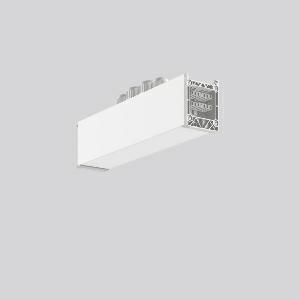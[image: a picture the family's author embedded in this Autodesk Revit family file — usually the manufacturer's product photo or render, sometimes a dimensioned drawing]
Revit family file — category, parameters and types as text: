
# Revit family: linedo_mitteleinspeisung_14pol_b_b_982698_002_1_c4a3
name_source: partatom
category: Lighting Fixtures
units: mm (PartAtom-declared; Revit-internal decimal feet)

## family parameters
Cut with Voids When Loaded = No
Host = Face
Light Source = No
Part Type = Normal
Room Calculation Point = No
Round Connector Dimension = Use Diameter
Shared = No

## types (1)
- LINEDO_Mitteleinspeisung_14pol_B_B
    Apparent Load = 0 VA
    Default Elevation = 1800 mm
    Description = Series: LINEDO
Middle power feed, 14-pole, connection socket / socket. Housing: extruded aluminium profile, powder-coated. Cover made of plastic, surface like housing. LINEDO plug system, plastic, light grey. 4 cable glands (2 x M20 and 2 x M25). Cable glands on top. Easy connection for rigid or flexible wires.
Colour: white
Length: 312 mm
Width: 58 mm
Height: 76 mm
Weight: 850 g
    Height = 76 mm
    Lamp = 0 x
    Length = 312 mm
    Luminous efficacy = 0 lm/W
    Manufacturer = RZB
    ModVariant = No
    Model = 982698.002.1
    Mounting Place = Ceiling
    Mounting Type = Surface mounted, Pendant
    Number of Poles = 1
    OnlyDefault = Yes
    Power Factor = 1
    Product Name = LINEDO_Mitteleinspeisung_14pol_B_B
    Product group = Surface mounted continuous line luminaire system
    ProductGroupID = 310
    Protection Class = Protection class I
    Protection Degree = IP 54
    RLX_Detail_Level = 1
    RLX_Emergency_Light_Flux = 0 lm
    RLX_Emergency_Type = 0
    RLX_Emergency_Type_DB = No
    RlxData = <blob elided: 20853 chars, md5=1e5872ce>
    Standby Power = 0 W
    System Light Flux = 0 lm
    System Power = 0 W
    Type Comments = Product without accessories
    Type Image = 982698.002.1.jpg
    URL = http://relux.com
    VarID = ---
    Voltage = 0 V
    Weight = 0.00 kg
    Width = 58 mm

## geometry (parser evidence)
native form markers: Blend x4, Sweep x11
no freeform markers — native parametric forms only
